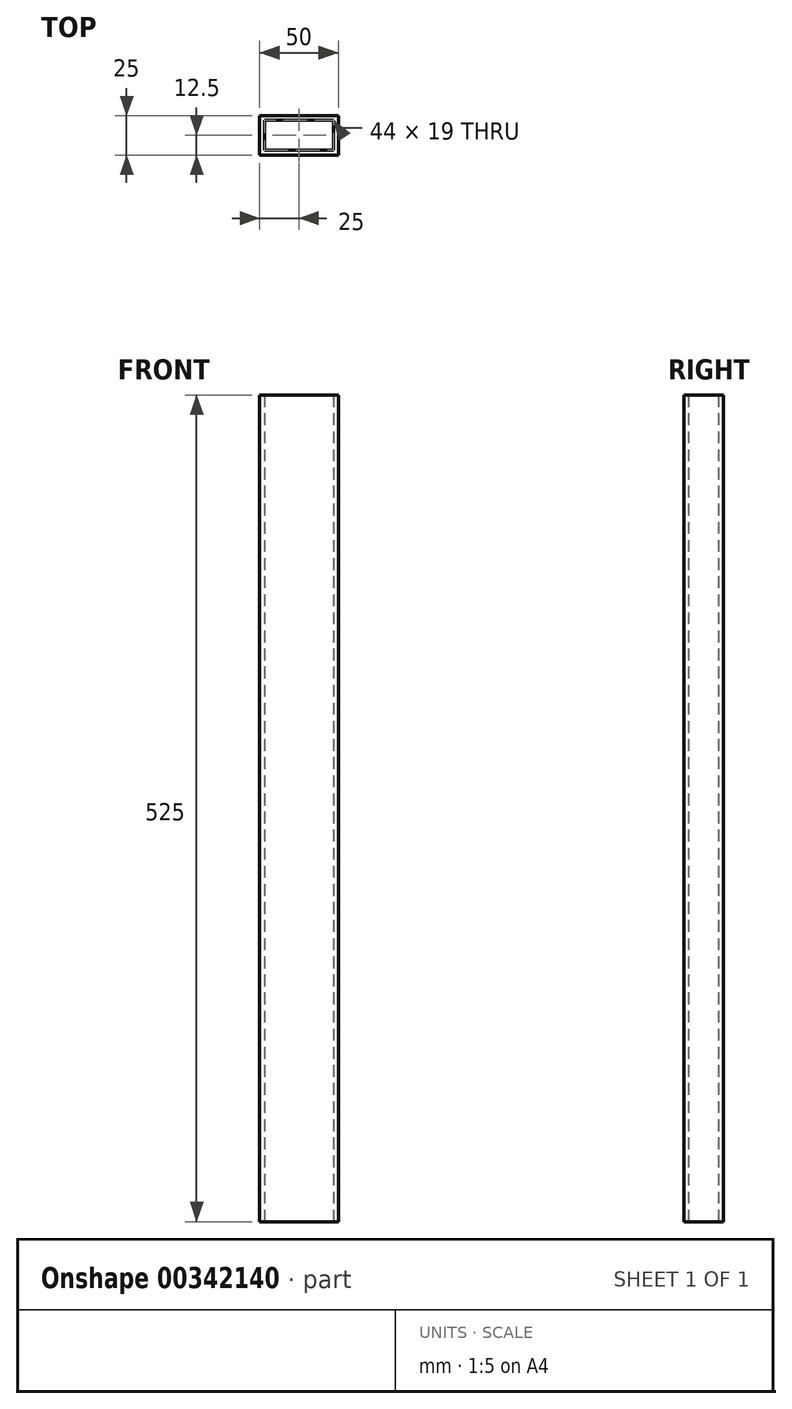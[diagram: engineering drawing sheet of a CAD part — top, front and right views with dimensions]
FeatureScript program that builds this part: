
annotation { "Feature Type Name" : "Feature", "Feature Type Description" : "" }
export const myFeature = defineFeature(function(context is Context, id is Id, definition is map)
    precondition{}
    {
        {
            var Q0;
            Q0=qCreatedBy(makeId("Top.planeOp"),FACE);
            var sketch = newSketch(context, id + "F0", { "sketchPlane" : qUnion([Q0])});
            skLineSegment(sketch, "E0.bottom", {"start": v(-25, -12.5) * mm, "end": v(25, -12.5) * mm});
            skLineSegment(sketch, "E0.top", {"start": v(-25, 12.5) * mm, "end": v(25, 12.5) * mm});
            skLineSegment(sketch, "E0.left", {"start": v(-25, -12.5) * mm, "end": v(-25, 12.5) * mm});
            skLineSegment(sketch, "E0.right", {"start": v(25, -12.5) * mm, "end": v(25, 12.5) * mm});
            skPoint(sketch, "E0.middle", {"position": v(0, 0) * mm});
            skLineSegment(sketch, "E1.bottom", {"start": v(-22, -9.5) * mm, "end": v(22, -9.5) * mm});
            skLineSegment(sketch, "E1.top", {"start": v(-22, 9.5) * mm, "end": v(22, 9.5) * mm});
            skLineSegment(sketch, "E1.left", {"start": v(-22, -9.5) * mm, "end": v(-22, 9.5) * mm});
            skLineSegment(sketch, "E1.right", {"start": v(22, -9.5) * mm, "end": v(22, 9.5) * mm});
            skSolve(sketch);
        }
        {
            var Q0;
            Q0=makeQuery(id+"F0.imprint","IMPRINT",FACE,{"disambiguationData":[TD([[makeQuery(id+"F0.imprint","IMPRINT",EDGE,{"derivedFrom":sQuery(id+"F0.wireOp",EDGE,"E0.bottom")}),1.0]])]});
            extrude(context, id + "F1", {"entities" : qUnion([Q0]), "endBound" : BoundingType.SYMMETRIC, "depth" : 525 * mm});
        }
    });
